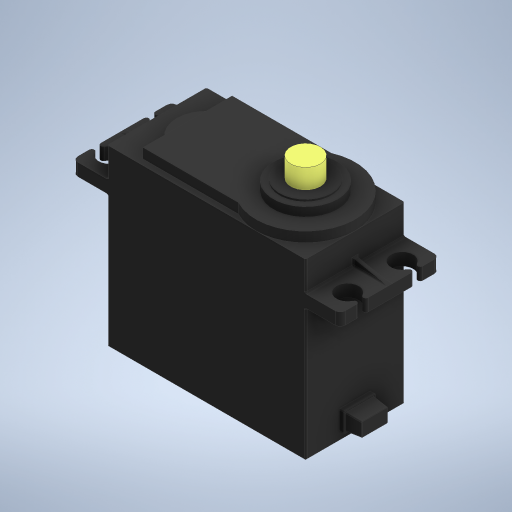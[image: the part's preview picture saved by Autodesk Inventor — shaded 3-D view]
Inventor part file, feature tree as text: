
AUTODESK INVENTOR PART (.ipt)
format: ipt  version: 2023.1 (Build 271208000, 208)  size: 565,760 bytes
history: native  units: mm
features: sketch x12, extrude x11, fillet x7, chamfer x5, other x2, projected_geometry x2, mirror x1
ambient origin geometry x8: Origin, YZ Plane, XZ Plane, XY Plane, X Axis, Y Axis, Z Axis, Center Point
bodies: Body1 (feature_tree)
feature tree (40):
  other  "솔리드1"
  extrude  "돌출1"  Depth=40.0mm
  other  "작업 평면1"
  extrude  "돌출2"  Depth=20.0mm
  extrude  "돌출3"  Depth=37.0mm TaperAngle=0.0deg
  extrude  "돌출4"  [1 undecoded]
  mirror  "미러1"
  extrude  "돌출5"  Depth=54.0mm
  extrude  "돌출6"  Depth=2.5mm TaperAngle=0.0deg
  sketch  "스케치7"
  extrude  "돌출7"  Depth=4.5mm
  extrude  "돌출8"  Depth=4.5mm
  extrude  "돌출9"  Depth=3.0mm
  fillet  "모깎기1"  Radius=1.0mm
  fillet  "모깎기2"  Radius=4.5mm
  chamfer  "모따기1"  [1 undecoded]
  fillet  "모깎기3"  Radius=1.4mm
  fillet  "모깎기4"  Radius=0.7mm
  fillet  "모깎기5"  Radius=10.0mm
  extrude  "돌출10"  Depth=20.0mm
  extrude  "돌출11"  Depth=18.0mm
  chamfer  "모따기2"  Distance=6.0mm
  chamfer  "모따기3"  Distance=2.0mm
  chamfer  "모따기4"  Distance=2.0mm
  chamfer  "모따기5"  Distance=4.5mm
  fillet  "모깎기6"  Radius=9.0mm
  fillet  "모깎기7"  Radius=1.7mm
  sketch  "스케치13"
  sketch  "스케치14"
  sketch  "스케치1"
  sketch  "스케치2"
  sketch  "스케치3"
  sketch  "스케치4"
  sketch  "스케치5"
  sketch  "스케치6"
  sketch  "스케치8"
  projected_geometry  "투영된 루프1"
  sketch  "스케치9"
  sketch  "스케치10"
  projected_geometry  "투영된 루프2"
note: 2 required parameter values undecoded (feature->parameter linkage not recoverable at this tier; creation-order binding heuristic only, values carry confidence <= 0.55)
